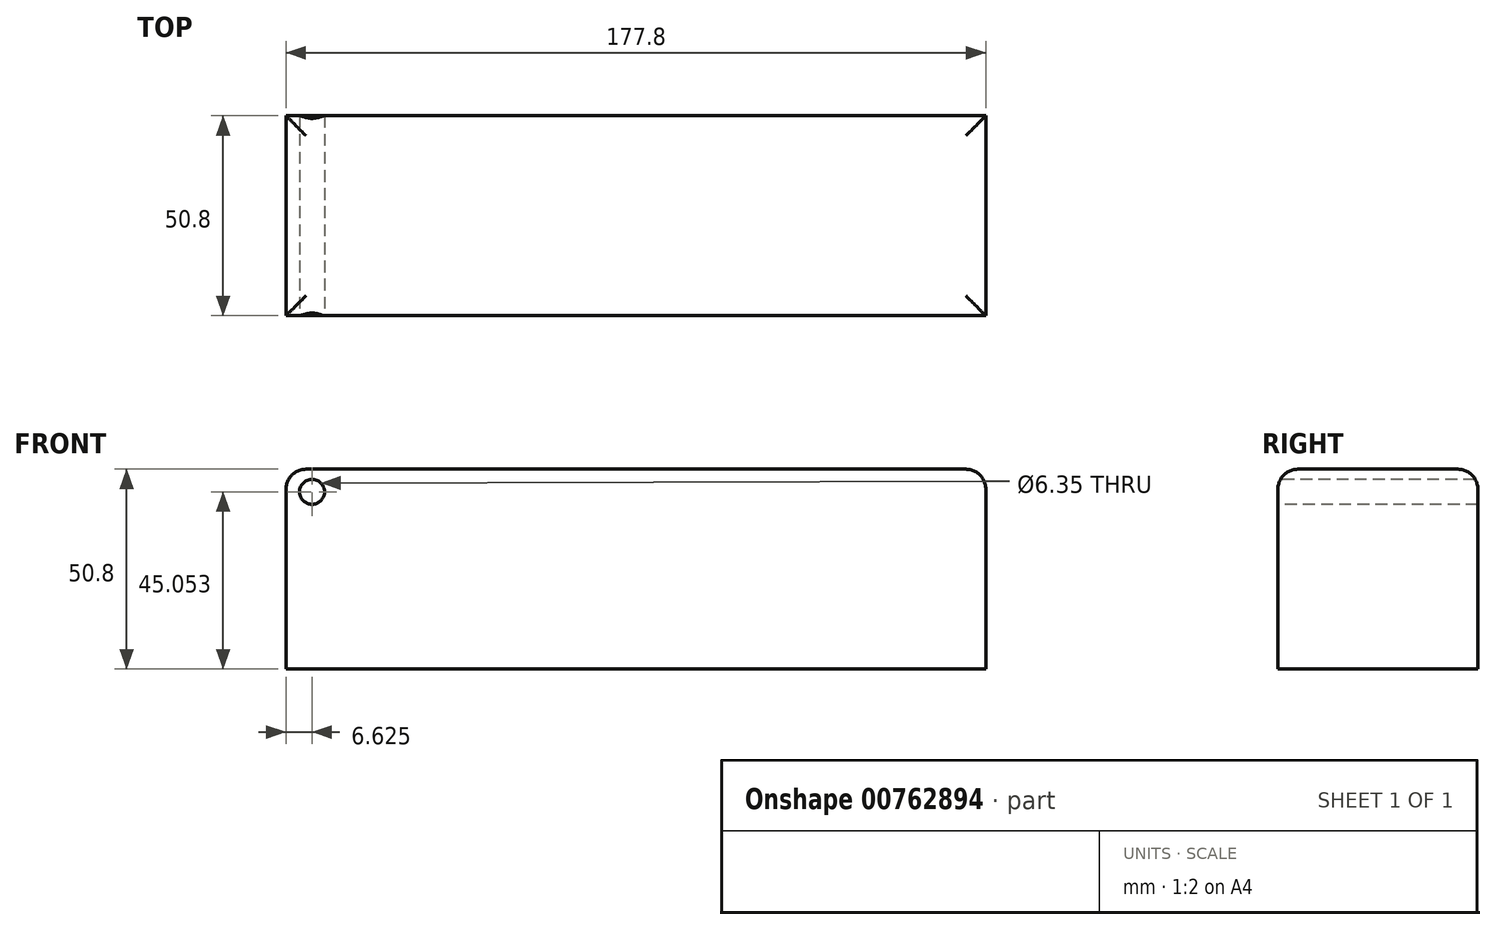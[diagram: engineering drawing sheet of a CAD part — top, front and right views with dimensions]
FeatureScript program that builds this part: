
annotation { "Feature Type Name" : "Feature", "Feature Type Description" : "" }
export const myFeature = defineFeature(function(context is Context, id is Id, definition is map)
    precondition{}
    {
        {
            var Q0;
            Q0=qCreatedBy(makeId("Front.planeOp"),FACE);
            var sketch = newSketch(context, id + "F0", { "sketchPlane" : qUnion([Q0])});
            skLineSegment(sketch, "E0.bottom", {"start": v(25.4, -25.4) * mm, "end": v(-25.4, -25.4) * mm});
            skLineSegment(sketch, "E0.top", {"start": v(25.4, 25.4) * mm, "end": v(-25.4, 25.4) * mm});
            skLineSegment(sketch, "E0.left", {"start": v(25.4, -25.4) * mm, "end": v(25.4, 25.4) * mm});
            skLineSegment(sketch, "E0.right", {"start": v(-25.4, -25.4) * mm, "end": v(-25.4, 25.4) * mm});
            skPoint(sketch, "E0.middle", {"position": v(0, 0) * mm});
            skSolve(sketch);
        }
        {
            var Q0;
            Q0=makeQuery(id+"F0.imprint","IMPRINT",FACE,{"disambiguationData":[TD([[makeQuery(id+"F0.imprint","IMPRINT",EDGE,{"derivedFrom":sQuery(id+"F0.wireOp",EDGE,"E0.bottom")}),-1.0]])]});
            extrude(context, id + "F1", {"entities" : qUnion([Q0]), "depth" : 50.8 * mm, "offsetDistance" : 25.4 * mm});
        }
        {
            var Q0;
            Q0=makeQuery(id+"F1.opExtrude","SWEPT_FACE",FACE,{"disambiguationData":[OSD([sQuery(id+"F0.wireOp",EDGE,"E0.left")])]});
            extrude(context, id + "F2", {"entities" : qUnion([Q0]), "operationType" : NewBodyOperationType.ADD, "depth" : 127 * mm, "offsetDistance" : 25.4 * mm});
        }
        {
            var Q0;
            {var subQ0=sQuery(id+"F0.wireOp",EDGE,"E0.left");Q0=makeQuery(id+"F2.boolean.opBoolean","MERGE",FACE,{"derivedFrom":[makeQuery(id+"F1.opExtrude","CAP_FACE",FACE,{"disambiguationData":[OSD([sQuery(id+"F0.wireOp",EDGE,"E0.bottom"),sQuery(id+"F0.wireOp",EDGE,"E0.top"),subQ0,sQuery(id+"F0.wireOp",EDGE,"E0.right")])],"isStart":false}),makeQuery(id+"F2.opExtrude","SWEPT_FACE",FACE,{"disambiguationData":[OSD([subQ0]),TDD([makeQuery(id+"F1.opExtrude","CAP_EDGE",EDGE,{"disambiguationData":[OSD([subQ0])],"isStart":false})])]})]});}
            var sketch = newSketch(context, id + "F3", { "sketchPlane" : qUnion([Q0])});
            skCircle(sketch, "E1", {"center": v(-18.77, 19.65) * mm, "radius": 2.26 * mm});
            skSolve(sketch);
        }
        {
            var Q0;
            Q0=sQuery(id+"F3.wireOp",VERTEX,"E1.center");
            var Q1;
            Q1=makeQuery(id+"F1.opExtrude","SWEPT_BODY",BODY,{"disambiguationData":[OSD([sQuery(id+"F0.wireOp",EDGE,"E0.bottom"),sQuery(id+"F0.wireOp",EDGE,"E0.top"),sQuery(id+"F0.wireOp",EDGE,"E0.left"),sQuery(id+"F0.wireOp",EDGE,"E0.right")])]});
            hole(context, id + "F4", {"style" : HoleStyle.SIMPLE, "endStyle" : HoleEndStyle.THROUGH, "holeDiameter" : 6.35 * mm, "majorDiameter" : 6.35 * mm, "isTappedThrough" : true, "tappedDepth" : 12.7 * mm, "tapClearance" : 3, "locations" : qUnion([Q0]), "scope" : qUnion([Q1])});
        }
        {
            var Q0;
            {var subQ0=sQuery(id+"F0.wireOp",EDGE,"E0.top");Q0=makeQuery(id+"F2.boolean.opBoolean","MERGE",FACE,{"derivedFrom":[makeQuery(id+"F1.opExtrude","SWEPT_FACE",FACE,{"disambiguationData":[OSD([subQ0])]}),makeQuery(id+"F2.opExtrude","SWEPT_FACE",FACE,{"disambiguationData":[OSD([subQ0,sQuery(id+"F0.wireOp",EDGE,"E0.left")])]})]});}
            fillet(context, id + "F5", {"entities" : qUnion([Q0]), "radius" : 5.08 * mm, "allowEdgeOverflow" : false});
        }
    });
